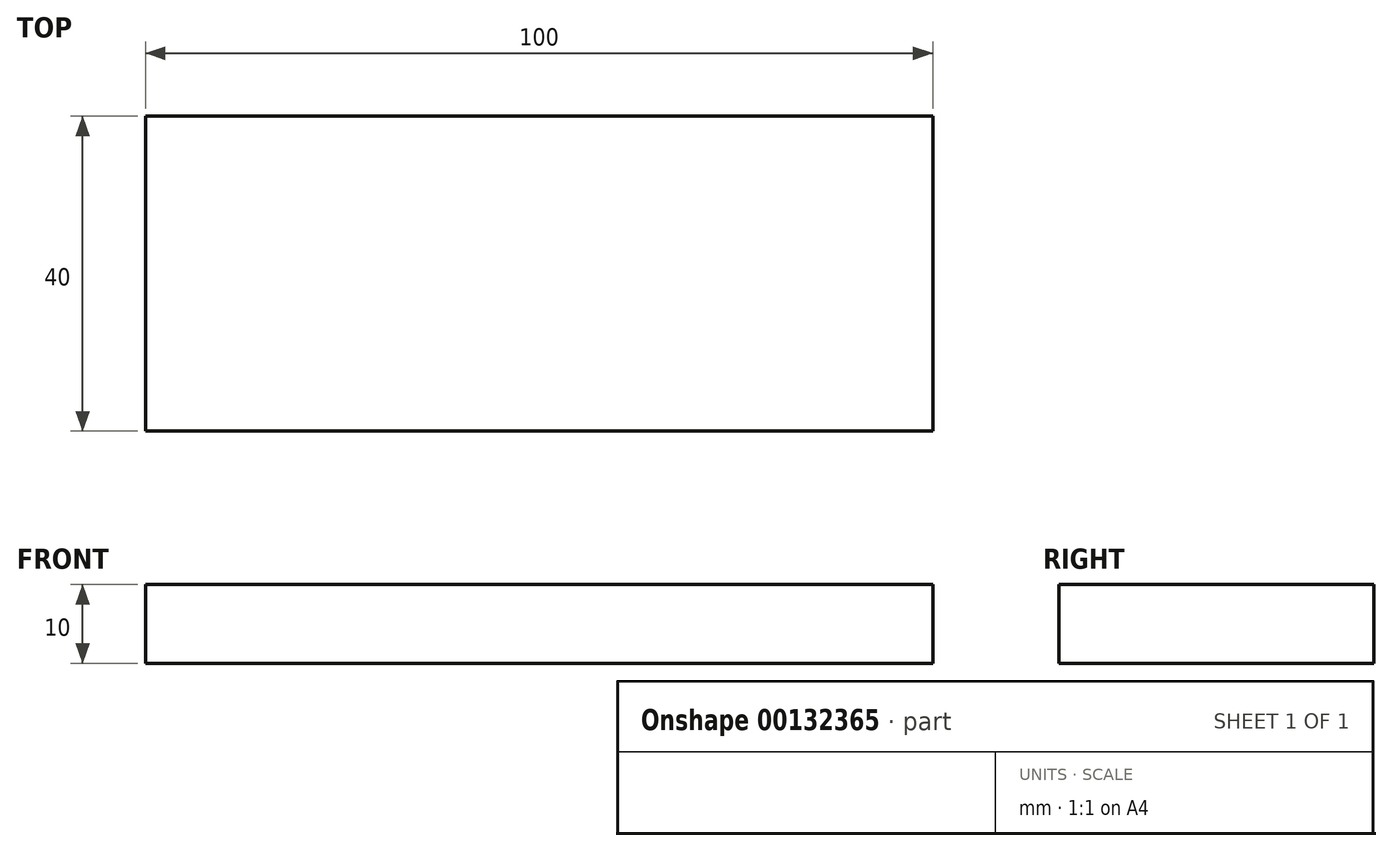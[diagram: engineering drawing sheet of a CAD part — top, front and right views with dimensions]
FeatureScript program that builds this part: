
annotation { "Feature Type Name" : "Feature", "Feature Type Description" : "" }
export const myFeature = defineFeature(function(context is Context, id is Id, definition is map)
    precondition{}
    {
        {
            var Q0;
            Q0=qCreatedBy(makeId("Top.planeOp"),FACE);
            var sketch = newSketch(context, id + "F0", { "sketchPlane" : qUnion([Q0])});
            skLineSegment(sketch, "E0.bottom", {"start": v(-75, 31.43) * mm, "end": v(25, 31.43) * mm});
            skLineSegment(sketch, "E0.top", {"start": v(-75, -8.57) * mm, "end": v(25, -8.57) * mm});
            skLineSegment(sketch, "E0.left", {"start": v(-75, 31.43) * mm, "end": v(-75, -8.57) * mm});
            skLineSegment(sketch, "E0.right", {"start": v(25, 31.43) * mm, "end": v(25, -8.57) * mm});
            skSolve(sketch);
        }
        {
            var Q0;
            Q0 = qSketchRegion(id + "F0", true);
            extrude(context, id + "F1", {"entities" : qUnion([Q0]), "depth" : 10 * mm});
        }
    });
